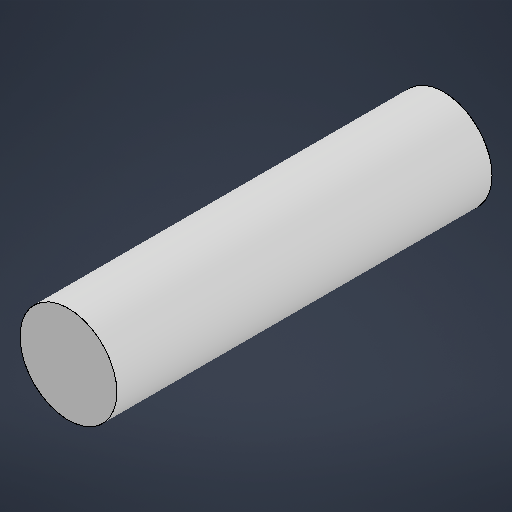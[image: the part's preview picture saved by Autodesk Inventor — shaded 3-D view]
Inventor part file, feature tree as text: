
AUTODESK INVENTOR PART (.ipt)
format: ipt  version: 2025.3 (Build 293356000, 356)  size: 169,472 bytes
history: native  units: mm
features: extrude x1, sketch x1
ambient origin geometry x8: Origin, YZ Plane, XZ Plane, XY Plane, X Axis, Y Axis, Z Axis, Center Point
bodies: Solid1 (feature_tree)
feature tree (2):
  extrude  "Extrusion1"  Depth=11.619mm TaperAngle=0.0deg
  sketch  "Sketch1"  dims[d0=3.0mm d1=11.619mm d2=0.0mm]
